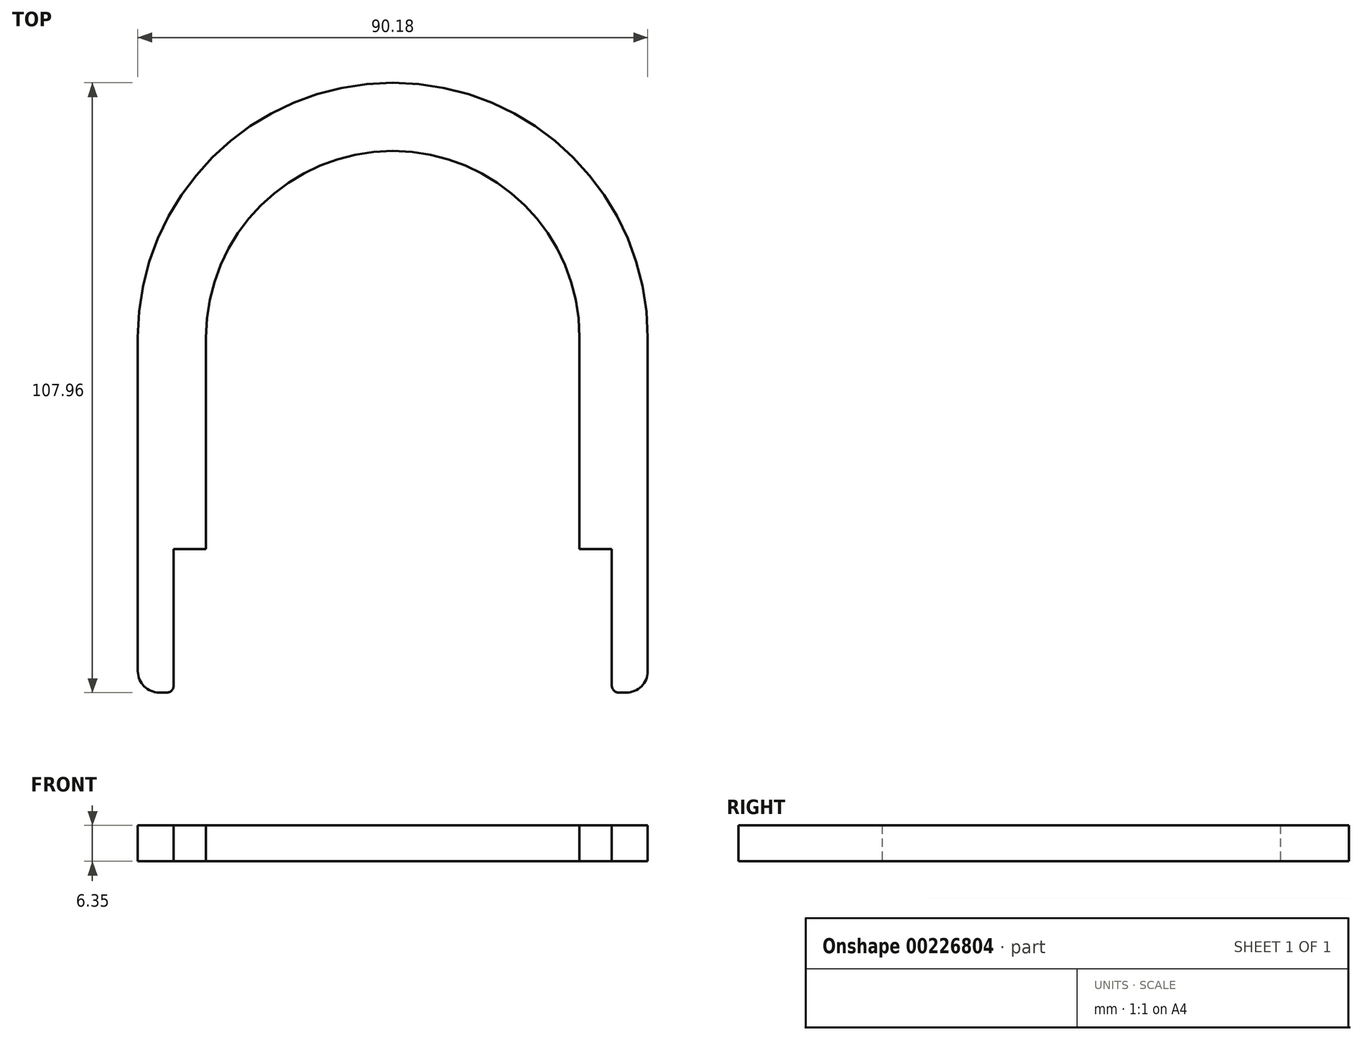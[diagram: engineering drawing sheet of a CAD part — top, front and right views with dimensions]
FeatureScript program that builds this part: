
annotation { "Feature Type Name" : "Feature", "Feature Type Description" : "" }
export const myFeature = defineFeature(function(context is Context, id is Id, definition is map)
    precondition{}
    {
        {
            var Q0;
            Q0=qCreatedBy(makeId("Top.planeOp"),FACE);
            var sketch = newSketch(context, id + "F0", { "sketchPlane" : qUnion([Q0])});
            skArc(sketch, "E0", {"start": v(45.09, 0) * mm, "mid": v(0, 45.09) * mm, "end": v(-45.09, 0) * mm});
            skLineSegment(sketch, "E1", {"start": v(45.09, 0) * mm, "end": v(45.09, -62.87) * mm});
            skLineSegment(sketch, "E2", {"start": v(45.09, -62.87) * mm, "end": v(38.74, -62.87) * mm});
            skLineSegment(sketch, "E3", {"start": v(38.74, -62.87) * mm, "end": v(38.74, -37.46) * mm});
            skLineSegment(sketch, "E4", {"start": v(38.73, -37.46) * mm, "end": v(33.02, -37.47) * mm});
            skLineSegment(sketch, "E5", {"start": v(33.02, -37.47) * mm, "end": v(33.02, 0) * mm});
            skArc(sketch, "E6", {"start": v(33.02, 0) * mm, "mid": v(0, 33.02) * mm, "end": v(-33.02, 0) * mm});
            skLineSegment(sketch, "E7", {"start": v(0, 0) * mm, "end": v(0, -139.48) * mm, "construction": true});
            skLineSegment(sketch, "E8.MirrorCS", {"start": v(-45.09, -62.87) * mm, "end": v(-38.74, -62.87) * mm});
            skLineSegment(sketch, "E9.MirrorCS", {"start": v(-38.74, -37.47) * mm, "end": v(-33.02, -37.47) * mm});
            skArc(sketch, "E10.MirrorCS", {"start": v(-45.09, 0) * mm, "mid": v(0, 45.09) * mm, "end": v(45.09, 0) * mm});
            skLineSegment(sketch, "E11.MirrorCS", {"start": v(-45.09, 0) * mm, "end": v(-45.09, -62.87) * mm});
            skArc(sketch, "E12.MirrorC", {"start": v(-33.02, 0) * mm, "mid": v(0, 33.02) * mm, "end": v(33.02, 0) * mm});
            skLineSegment(sketch, "E13.MirrorCS", {"start": v(-38.74, -62.87) * mm, "end": v(-38.74, -37.47) * mm});
            skLineSegment(sketch, "E14.MirrorCS", {"start": v(-33.02, -37.47) * mm, "end": v(-33.02, 0) * mm});
            skPoint(sketch, "E15", {"position": v(0, 45.09) * mm});
            skSolve(sketch);
        }
        {
            var Q0;
            Q0=makeQuery(id+"F0.imprint","IMPRINT",FACE,{"disambiguationData":[TD([[makeQuery(id+"F0.imprint","IMPRINT",EDGE,{"derivedFrom":sQuery(id+"F0.wireOp",EDGE,"E1")}),-1.0]])]});
            extrude(context, id + "F1", {"entities" : qUnion([Q0]), "depth" : 6.35 * mm});
        }
        {
            var Q0;
            Q0=makeQuery(id+"F1.opExtrude","SWEPT_EDGE",EDGE,{"disambiguationData":[OSD([sQuery(id+"F0.wireOp",EDGE,"E8.MirrorCS"),sQuery(id+"F0.wireOp",EDGE,"E11.MirrorCS")])]});
            var Q1;
            Q1=makeQuery(id+"F1.opExtrude","SWEPT_EDGE",EDGE,{"disambiguationData":[OSD([sQuery(id+"F0.wireOp",EDGE,"E1"),sQuery(id+"F0.wireOp",EDGE,"E2")])]});
            fillet(context, id + "F2", {"entities" : qUnion([Q0, Q1]), "radius" : 3.8 * mm, "tangentPropagation" : true, "allowEdgeOverflow" : false});
        }
        {
            var Q0;
            Q0=makeQuery(id+"F1.opExtrude","SWEPT_EDGE",EDGE,{"disambiguationData":[OSD([sQuery(id+"F0.wireOp",EDGE,"E8.MirrorCS"),sQuery(id+"F0.wireOp",EDGE,"E13.MirrorCS")])]});
            var Q1;
            Q1=makeQuery(id+"F1.opExtrude","SWEPT_EDGE",EDGE,{"disambiguationData":[OSD([sQuery(id+"F0.wireOp",EDGE,"E2"),sQuery(id+"F0.wireOp",EDGE,"E3")])]});
            fillet(context, id + "F3", {"entities" : qUnion([Q0, Q1]), "radius" : 1.27 * mm, "tangentPropagation" : true, "allowEdgeOverflow" : false});
        }
    });
